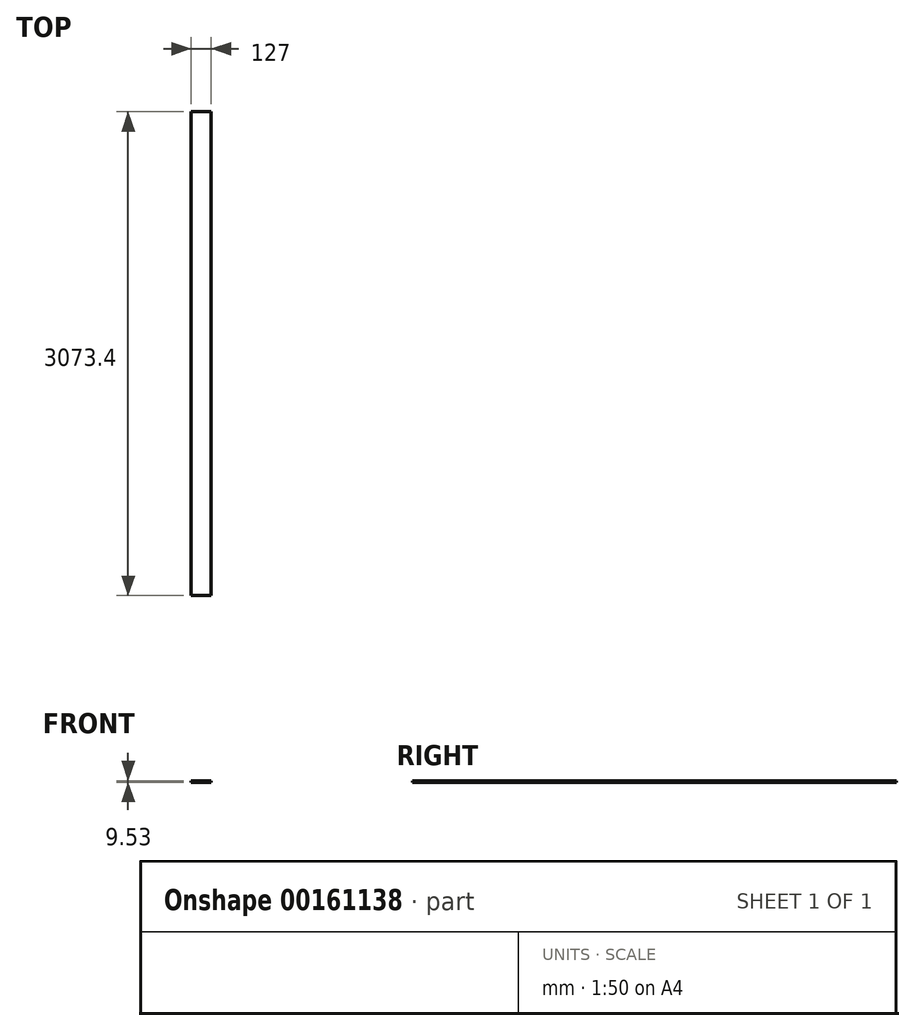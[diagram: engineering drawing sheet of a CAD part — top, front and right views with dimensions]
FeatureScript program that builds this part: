
annotation { "Feature Type Name" : "Feature", "Feature Type Description" : "" }
export const myFeature = defineFeature(function(context is Context, id is Id, definition is map)
    precondition{}
    {
        {
            var Q0;
            Q0=qCreatedBy(makeId("Front.planeOp"),FACE);
            var sketch = newSketch(context, id + "F0", { "sketchPlane" : qUnion([Q0])});
            skLineSegment(sketch, "E0.bottom", {"start": v(0, 0) * mm, "end": v(127, 0) * mm});
            skLineSegment(sketch, "E0.top", {"start": v(0, 9.53) * mm, "end": v(127, 9.53) * mm});
            skLineSegment(sketch, "E0.left", {"start": v(0, 0) * mm, "end": v(0, 9.53) * mm});
            skLineSegment(sketch, "E0.right", {"start": v(127, 0) * mm, "end": v(127, 9.53) * mm});
            skSolve(sketch);
        }
        {
            var Q0;
            Q0=makeQuery(id+"F0.imprint","IMPRINT",FACE,{"disambiguationData":[TD([[makeQuery(id+"F0.imprint","IMPRINT",EDGE,{"derivedFrom":sQuery(id+"F0.wireOp",EDGE,"E0.bottom")}),1.0]])]});
            extrude(context, id + "F1", {"entities" : qUnion([Q0]), "depth" : 3073.4 * mm});
        }
    });
